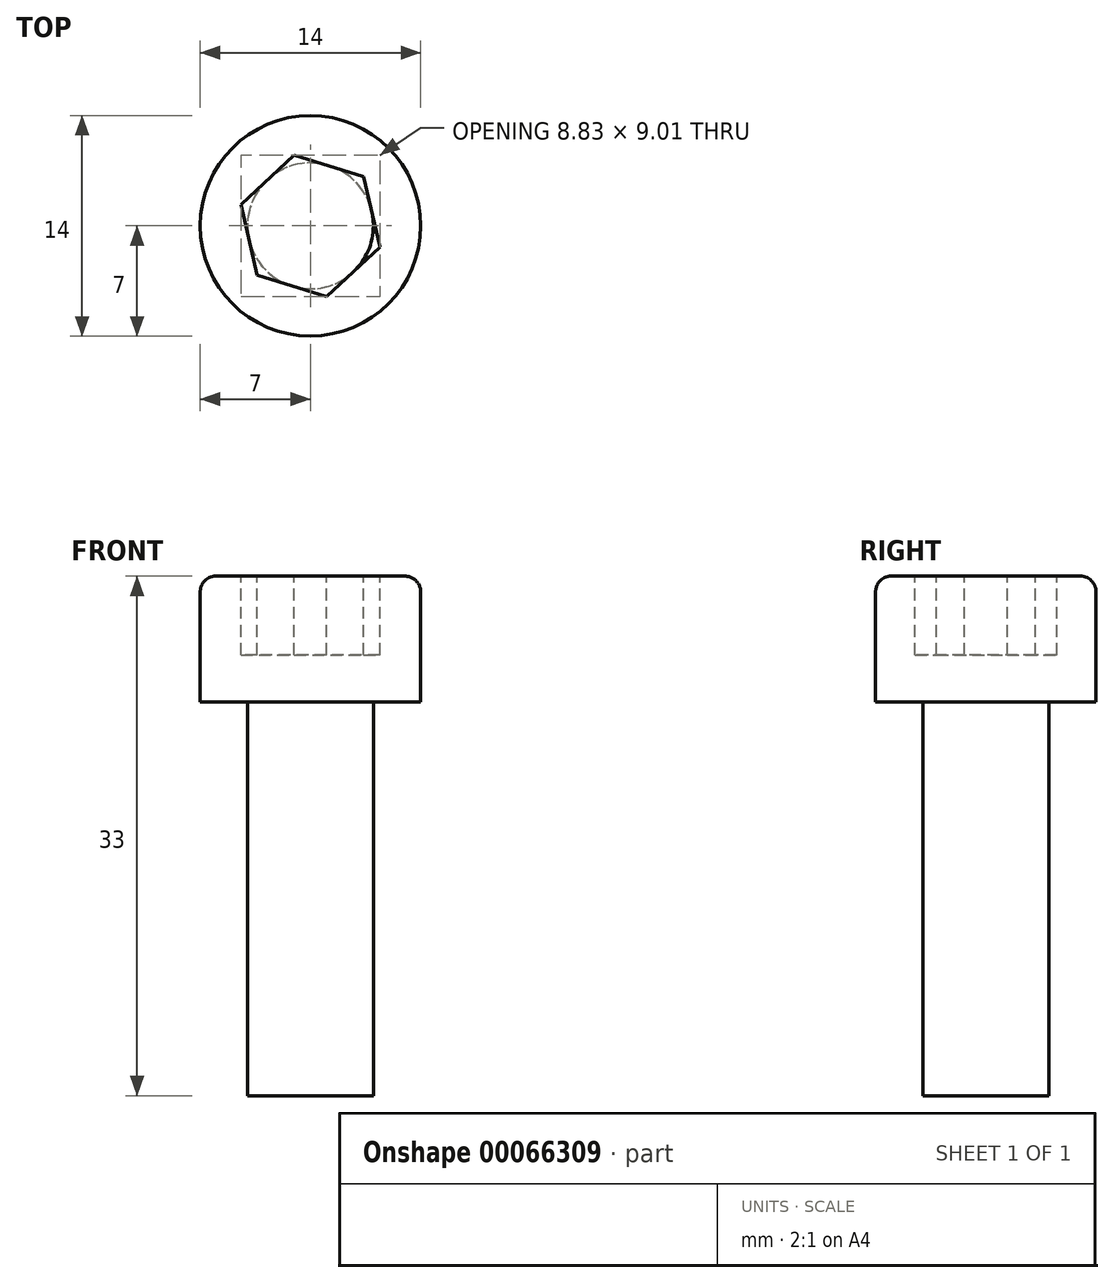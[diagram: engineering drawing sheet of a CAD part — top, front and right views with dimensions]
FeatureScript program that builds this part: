
annotation { "Feature Type Name" : "Feature", "Feature Type Description" : "" }
export const myFeature = defineFeature(function(context is Context, id is Id, definition is map)
    precondition{}
    {
        {
            var Q0;
            Q0=qCreatedBy(makeId("Top.planeOp"),FACE);
            var sketch = newSketch(context, id + "F0", { "sketchPlane" : qUnion([Q0])});
            skCircle(sketch, "E0", {"center": v(0, 0) * mm, "radius": 4 * mm});
            skSolve(sketch);
        }
        {
            var Q0;
            Q0 = qSketchRegion(id + "F0", true);
            extrude(context, id + "F4", {"entities" : qUnion([Q0]), "depth" : 25 * mm});
        }
        {
            var Q0;
            Q0=makeQuery(id+"F4.opExtrude","CAP_FACE",FACE,{"disambiguationData":[OSD([sQuery(id+"F0.wireOp",EDGE,"E0")])],"isStart":false});
            var sketch = newSketch(context, id + "F1", { "sketchPlane" : qUnion([Q0])});
            skCircle(sketch, "E1", {"center": v(0, 0) * mm, "radius": 7 * mm});
            skSolve(sketch);
        }
        {
            var Q0;
            Q0=makeQuery(id+"F1.imprint","IMPRINT",FACE,{"disambiguationData":[TD([[makeQuery(id+"F1.imprint","IMPRINT",EDGE,{"derivedFrom":sQuery(id+"F1.wireOp",EDGE,"E1")}),1.0]])]});
            var Q1;
            Q1=makeQuery(id+"F1.imprint","IMPRINT",FACE,{"disambiguationData":[TD([[makeQuery(id+"F1.imprint","IMPRINT",EDGE,{"derivedFrom":makeQuery(id+"F4.opExtrude","CAP_EDGE",EDGE,{"disambiguationData":[OSD([sQuery(id+"F0.wireOp",EDGE,"E0")])],"isStart":false})}),1.0]])]});
            var Q2;
            Q2=sQuery(id+"F1.wireOp",EDGE,"E1");
            var Q3;
            Q3 = qBodyType(qCreatedBy(id + "F1" ,EDGE), BodyType.WIRE);
            extrude(context, id + "F5", {"entities" : qUnion([Q0, Q1]), "surfaceEntities" : qUnion([Q2, Q3]), "depth" : 8 * mm});
        }
        {
            var Q0;
            Q0=makeQuery(id+"F5.opExtrude","CAP_FACE",FACE,{"disambiguationData":[OSD([sQuery(id+"F1.wireOp",EDGE,"E1")])],"isStart":false});
            var sketch = newSketch(context, id + "F6", { "sketchPlane" : qUnion([Q0])});
            skCircle(sketch, "E2.cCircle", {"center": v(0, 0) * mm, "radius": 4 * mm, "construction": true});
            skLineSegment(sketch, "E2.0", {"start": v(4.41, -1.36) * mm, "end": v(1.03, -4.5) * mm});
            skLineSegment(sketch, "E2.1", {"start": v(1.03, -4.5) * mm, "end": v(-3.39, -3.14) * mm});
            skLineSegment(sketch, "E2.2", {"start": v(-3.39, -3.14) * mm, "end": v(-4.41, 1.36) * mm});
            skLineSegment(sketch, "E2.3", {"start": v(-4.41, 1.36) * mm, "end": v(-1.03, 4.5) * mm});
            skLineSegment(sketch, "E2.4", {"start": v(-1.03, 4.5) * mm, "end": v(3.39, 3.14) * mm});
            skLineSegment(sketch, "E2.5", {"start": v(3.39, 3.14) * mm, "end": v(4.41, -1.36) * mm});
            skPoint(sketch, "E2.0.midPoint", {"position": v(2.72, -2.93) * mm});
            skSolve(sketch);
        }
        {
            var Q0;
            Q0=makeQuery(id+"F6.imprint","IMPRINT",FACE,{"disambiguationData":[TD([[makeQuery(id+"F6.imprint","IMPRINT",EDGE,{"derivedFrom":sQuery(id+"F6.wireOp",EDGE,"E2.0")}),-1.0]])]});
            var Q1;
            Q1=sQuery(id+"F6.wireOp",EDGE,"E2.2");
            extrude(context, id + "F2", {"entities" : qUnion([Q0]), "operationType" : NewBodyOperationType.REMOVE, "surfaceEntities" : qUnion([Q1]), "oppositeDirection" : true, "depth" : 5 * mm});
        }
        {
            var Q0;
            Q0=makeQuery(id+"F5.opExtrude","CAP_EDGE",EDGE,{"disambiguationData":[OSD([sQuery(id+"F1.wireOp",EDGE,"E1")])],"isStart":false});
            fillet(context, id + "F3", {"entities" : qUnion([Q0]), "radius" : 1 * mm, "tangentPropagation" : true, "allowEdgeOverflow" : false});
        }
    });
